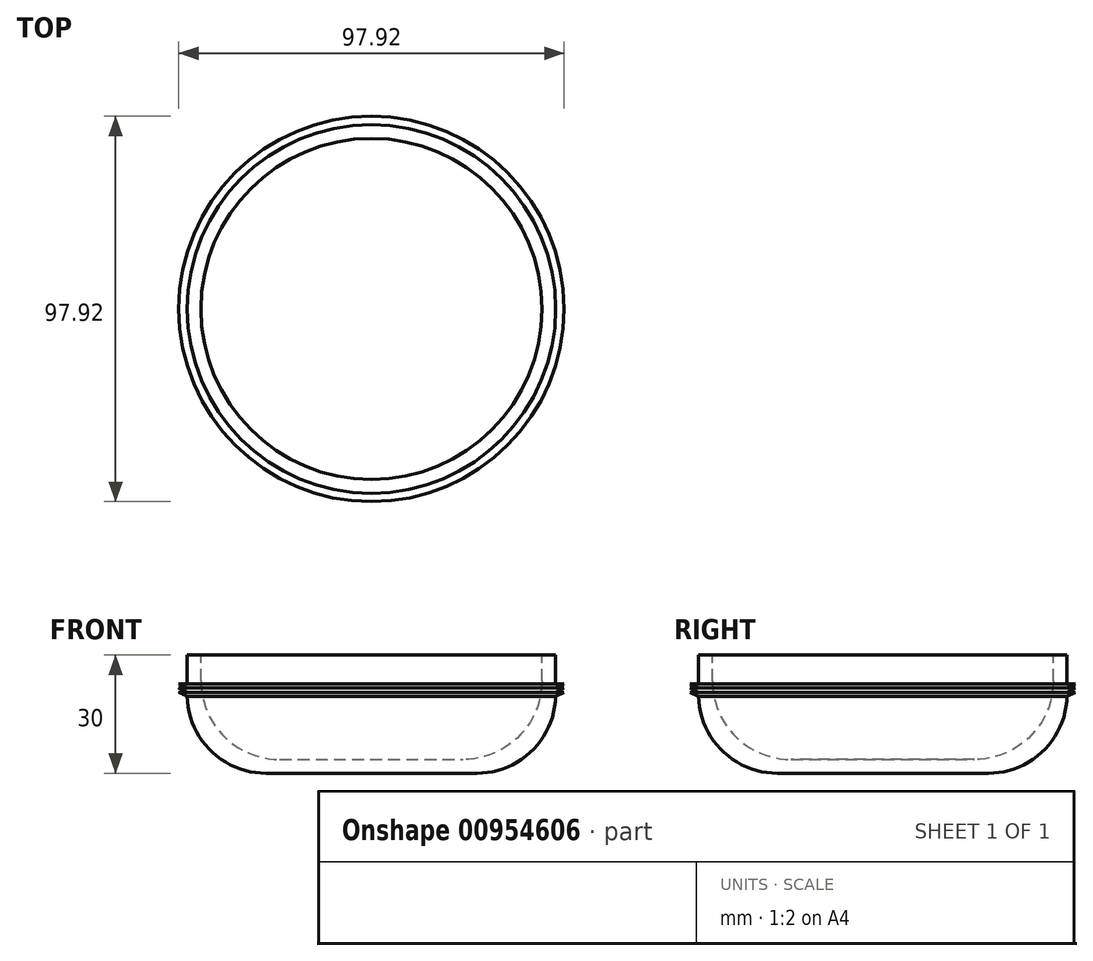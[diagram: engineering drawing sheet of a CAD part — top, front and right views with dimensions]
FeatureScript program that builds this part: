
annotation { "Feature Type Name" : "Feature", "Feature Type Description" : "" }
export const myFeature = defineFeature(function(context is Context, id is Id, definition is map)
    precondition{}
    {
        {
            var Q0;
            Q0=qCreatedBy(makeId("Front.planeOp"),FACE);
            var sketch = newSketch(context, id + "F0", { "sketchPlane" : qUnion([Q0])});
            skLineSegment(sketch, "E0", {"start": v(0, 0) * mm, "end": v(0, 30) * mm, "construction": true});
            skLineSegment(sketch, "E1", {"start": v(0, 0) * mm, "end": v(-26.8, 0) * mm});
            skLineSegment(sketch, "E2", {"start": v(-46.8, 19.96) * mm, "end": v(-46.82, 30) * mm});
            skLineSegment(sketch, "E3.0", {"start": v(-43.31, 23.46) * mm, "end": v(-43.32, 30) * mm});
            skLineSegment(sketch, "E3.1", {"start": v(0, 3.5) * mm, "end": v(-23.31, 3.5) * mm});
            skPoint(sketch, "E4.visualSharp", {"position": v(-46.77, 0) * mm});
            skArc(sketch, "E4.filletArc", {"start": v(-46.8, 19.96) * mm, "mid": v(-40.93, 5.84) * mm, "end": v(-26.8, 0) * mm});
            skPoint(sketch, "E5.visualSharp", {"position": v(-43.27, 3.5) * mm});
            skArc(sketch, "E5.filletArc", {"start": v(-43.31, 23.46) * mm, "mid": v(-37.44, 9.34) * mm, "end": v(-23.31, 3.5) * mm});
            skLineSegment(sketch, "E6", {"start": v(-46.82, 30) * mm, "end": v(-43.32, 30) * mm});
            skLineSegment(sketch, "E7", {"start": v(0, 3.5) * mm, "end": v(0, 0) * mm});
            skLineSegment(sketch, "E8", {"start": v(-46.8, 22.71) * mm, "end": v(-48.96, 22.7) * mm});
            skLineSegment(sketch, "E9", {"start": v(-48.96, 22.7) * mm, "end": v(-46.8, 21.65) * mm});
            skLineSegment(sketch, "E10", {"start": v(-46.8, 21.65) * mm, "end": v(-48.96, 21.65) * mm});
            skLineSegment(sketch, "E11", {"start": v(-48.96, 21.65) * mm, "end": v(-46.8, 20.6) * mm});
            skLineSegment(sketch, "E12", {"start": v(-46.8, 20.6) * mm, "end": v(-48.96, 20.6) * mm});
            skLineSegment(sketch, "E13", {"start": v(-48.96, 20.6) * mm, "end": v(-46.8, 19.54) * mm});
            skLineSegment(sketch, "E14", {"start": v(-46.8, 19.54) * mm, "end": v(-48.96, 19.53) * mm});
            skLineSegment(sketch, "E15", {"start": v(-48.96, 19.53) * mm, "end": v(-46.8, 18.47) * mm});
            skSolve(sketch);
        }
        {
            var Q0;
            Q0=makeQuery(id+"F0.imprint","IMPRINT",FACE,{"disambiguationData":[TD([[makeQuery(id+"F0.imprint","IMPRINT",EDGE,{"derivedFrom":sQuery(id+"F0.wireOp",EDGE,"E1")}),-1.0]])]});
            var Q1;
            {var subQ0=sQuery(id+"F0.wireOp",EDGE,"E8");Q1=makeQuery(id+"F0.imprint","IMPRINT",FACE,{"disambiguationData":[TD([[makeQuery(id+"F0.imprint","IMPRINT",EDGE,{"derivedFrom":subQ0}),1.0]])]});}
            var Q2;
            {var subQ0=sQuery(id+"F0.wireOp",EDGE,"E10");Q2=makeQuery(id+"F0.imprint","IMPRINT",FACE,{"disambiguationData":[TD([[makeQuery(id+"F0.imprint","IMPRINT",EDGE,{"derivedFrom":subQ0}),1.0]])]});}
            var Q3;
            {var subQ3=sQuery(id+"F0.wireOp",EDGE,"E12");Q3=makeQuery(id+"F0.imprint","IMPRINT",FACE,{"disambiguationData":[TD([[makeQuery(id+"F0.imprint","IMPRINT",EDGE,{"derivedFrom":subQ3}),1.0]])]});}
            var Q4;
            Q4=sQuery(id+"F0.wireOp",EDGE,"E0");
            revolve(context, id + "F1", {"surfaceOperationType" : NewSurfaceOperationType.NEW, "entities" : qUnion([Q0, Q1, Q2, Q3]), "axis" : qUnion([Q4]), "revolveType" : RevolveType.FULL});
        }
    });
